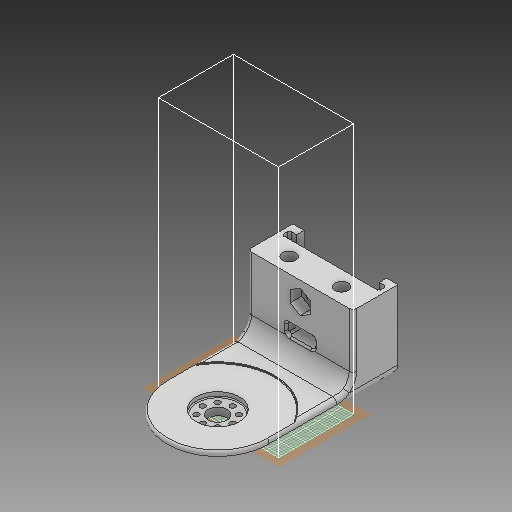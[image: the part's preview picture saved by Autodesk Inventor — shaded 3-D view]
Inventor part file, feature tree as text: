
AUTODESK INVENTOR PART (.ipt)
format: ipt  version: 2018 (Build 220112000, 112)  size: 965,632 bytes
history: native  units: mm
features: other x3, sketch x1, projected_geometry x1
ambient origin geometry x8: Origin, YZ Plane, XZ Plane, XY Plane, X Axis, Y Axis, Z Axis, Center Point
bodies: Solid1 (feature_tree)
feature tree (5):
  other  "arm_segment_1_1a2.ipt"
  sketch  "Sketch1"  dims[d0=10.0mm]
  other  "Solid1::arm_segment_1_1a2.ipt"
  other  "TaggingFeature1"
  projected_geometry  "Projected Loop1"
